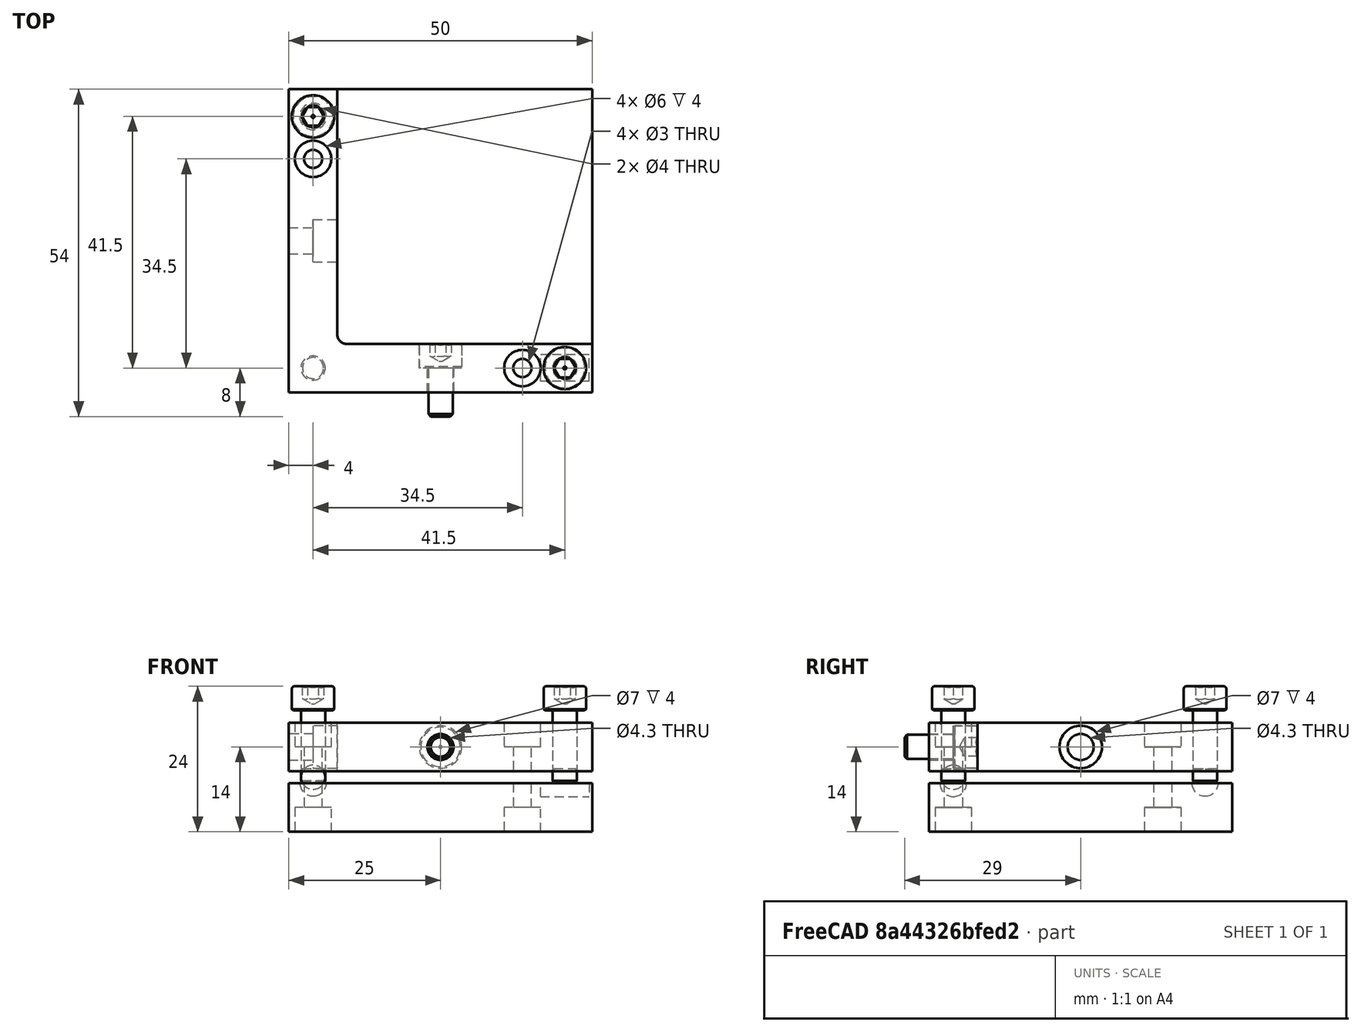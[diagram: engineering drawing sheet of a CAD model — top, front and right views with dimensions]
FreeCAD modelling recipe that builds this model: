
FCSTD DOCUMENT  (FreeCAD 0.21R33668 +7 (Git))
Label: KinematicMountBase_M4
License: All rights reserved
LicenseURL: https://en.wikipedia.org/wiki/All_rights_reserved
objects: Part::Cut×13, Part::Cylinder×13, Part::MultiFuse×6, Part::FeaturePython×5, Part::Sphere×4, Part::Box×3, Spreadsheet::Sheet×1, Part::Fillet×1
note: 45 computed .brp shape members not serialized (recipe doc carries the construction recipe); baked Part::Feature solids carry a one-line shape summary decoded from their .brp

FEATURE [Part::Box] Box  label="Cube"
  AttacherType = Attacher::AttachEngine3D
  Height = 8
  Length = 50
  Width = 50
  expr: Height = <<MountConfiguration>>.thickness
  expr: Length = <<MountConfiguration>>.outer_length
  expr: Width = <<MountConfiguration>>.outer_length
FEATURE [Spreadsheet::Sheet] Spreadsheet  label="MountConfiguration"
  cells = A2='Outer length; B2(outer_length)=50; A3='Holder width; B3(holder_width)=8; A4='Thickness; B4(thickness)=8
FEATURE [Part::Box] Box001  label="Cube001"
  AttacherType = Attacher::AttachEngine3D
  Height = 8
  Length = 42
  Placement = pos=(8,8,0) rot=(0,0,1;0rad)
  Width = 42
  expr: .Placement.Base.x = <<MountConfiguration>>.holder_width
  expr: .Placement.Base.y = <<MountConfiguration>>.holder_width
  expr: Height = <<MountConfiguration>>.thickness
  expr: Length = <<MountConfiguration>>.outer_length - <<MountConfiguration>>.holder_width
  expr: Width = <<MountConfiguration>>.outer_length - <<MountConfiguration>>.holder_width
FEATURE [Part::Cut] Cut
  Base = -> Box
  Tool = -> Box001
FEATURE [Part::FeaturePython] Screw  label="M4x8-Screw"  # Fasteners workbench fastener (typed FeaturePython)
  Placement = pos=(45.5,4,8) rot=(0,0,1;0rad)
  diameter = 5
  invert = false
  leftHanded = false
  length = 1
  lengthCustom = 8
  matchOuter = false
  offset = 0
  thread = false
  type = 47
  expr: .Placement.Base.x = <<MountConfiguration>>.outer_length - 7 / 2 - 1
  expr: .Placement.Base.y = <<MountConfiguration>>.holder_width / 2
  expr: .Placement.Base.z = <<MountConfiguration>>.thickness
FEATURE [Part::FeaturePython] Screw001  label="M4x8-Screw003"  # Fasteners workbench fastener (typed FeaturePython)
  Placement = pos=(4,45.5,8) rot=(0,0,1;0rad)
  diameter = 5
  invert = false
  leftHanded = false
  length = 1
  lengthCustom = 8
  matchOuter = false
  offset = 0
  thread = false
  type = 47
  expr: .Placement.Base.x = <<MountConfiguration>>.holder_width / 2
  expr: .Placement.Base.y = <<MountConfiguration>>.outer_length - 7 / 2 - 1
  expr: .Placement.Base.z = <<MountConfiguration>>.thickness
FEATURE [Part::Cylinder] Cylinder
  Angle = 360
  AttacherType = Attacher::AttachEngine3D
  FirstAngle = 0
  Height = 8
  Radius = 1.5
  SecondAngle = 0
  expr: Height = <<MountConfiguration>>.thickness
FEATURE [Part::Cylinder] Cylinder001
  Angle = 360
  AttacherType = Attacher::AttachEngine3D
  FirstAngle = 0
  Height = 4
  Placement = pos=(0,0,4) rot=(0,0,1;0rad)
  Radius = 3
  SecondAngle = 0
  expr: .Placement.Base.z = <<MountConfiguration>>.thickness / 2
  expr: Height = <<MountConfiguration>>.thickness / 2
FEATURE [Part::MultiFuse] Fusion  label="SpringHole1"
  Placement = pos=(38.5,4,0) rot=(0,0,1;0rad)
  Shapes = -> [Cylinder,Cylinder001]
  expr: .Placement.Base.x = <<MountConfiguration>>.outer_length - 7 / 2 - 1 - 1 * 7
  expr: .Placement.Base.y = <<MountConfiguration>>.holder_width / 2
FEATURE [Part::Cylinder] Cylinder002
  Angle = 360
  AttacherType = Attacher::AttachEngine3D
  FirstAngle = 0
  Height = 8
  Radius = 1.5
  SecondAngle = 0
  expr: Height = <<MountConfiguration>>.thickness
FEATURE [Part::Cylinder] Cylinder003
  Angle = 360
  AttacherType = Attacher::AttachEngine3D
  FirstAngle = 0
  Height = 4
  Placement = pos=(0,0,4) rot=(0,0,1;0rad)
  Radius = 3
  SecondAngle = 0
  expr: .Placement.Base.z = <<MountConfiguration>>.thickness / 2
  expr: Height = <<MountConfiguration>>.thickness / 2
FEATURE [Part::MultiFuse] Fusion001  label="SpringHole2"
  Placement = pos=(4,38.5,0) rot=(0,0,1;0rad)
  Shapes = -> [Cylinder002,Cylinder003]
  expr: .Placement.Base.x = <<MountConfiguration>>.holder_width / 2
  expr: .Placement.Base.y = <<MountConfiguration>>.outer_length - 7 / 2 - 1 - 1 * 7
FEATURE [Part::Cut] Cut001
  Base = -> Cut
  Tool = -> Fusion
FEATURE [Part::Cut] Cut002
  Base = -> Cut001
  Tool = -> Fusion001
FEATURE [Part::Cut] Cut003
  Base = -> Cut002
  Tool = -> Screw001
FEATURE [Part::Cut] Cut004
  Base = -> Cut003
  Tool = -> Screw
FEATURE [Part::FeaturePython] Screw002  label="M4x8-Screw004"  # Fasteners workbench fastener (typed FeaturePython)
  Placement = pos=(25,4,14) rot=(1,0,0;-1.5708rad)
  diameter = 5
  invert = false
  leftHanded = false
  length = 1
  lengthCustom = 8
  matchOuter = false
  offset = 0
  thread = false
  type = 47
  expr: .Placement.Base.x = <<MountConfiguration>>.outer_length / 2
  expr: .Placement.Base.y = <<MountConfiguration>>.holder_width - 4
  expr: .Placement.Base.z = <<MountConfiguration>>.thickness / 2 + <<MountConfiguration>>.thickness + 2
FEATURE [Part::Cylinder] Cylinder004
  Angle = 360
  AttacherType = Attacher::AttachEngine3D
  FirstAngle = 0
  Height = 4
  Radius = 3.5
  SecondAngle = 0
FEATURE [Part::Cylinder] Cylinder005
  Angle = 360
  AttacherType = Attacher::AttachEngine3D
  FirstAngle = 0
  Height = 8
  Radius = 2.15
  SecondAngle = 0
  expr: Height = <<MountConfiguration>>.holder_width
FEATURE [Part::MultiFuse] Fusion002
  Placement = pos=(25,8,4) rot=(0.242536,0,0;1.5708rad)
  Shapes = -> [Cylinder005,Cylinder004]
  expr: .Placement.Base.x = <<MountConfiguration>>.outer_length / 2
  expr: .Placement.Base.y = <<MountConfiguration>>.holder_width
  expr: .Placement.Base.z = <<MountConfiguration>>.thickness / 2
FEATURE [Part::Cut] Cut005
  Base = -> Cut004
  Tool = -> Fusion002
FEATURE [Part::Sphere] Sphere
  Angle1 = -90
  Angle2 = 90
  Angle3 = 360
  AttacherType = Attacher::AttachEngine3D
  Placement = pos=(4,4,-1) rot=(0,0,1;0rad)
  Radius = 2
  expr: .Placement.Base.x = <<MountConfiguration>>.holder_width / 2
  expr: .Placement.Base.y = <<MountConfiguration>>.holder_width / 2
FEATURE [Part::Cut] Cut006
  Base = -> Cut005
  Tool = -> Sphere
FEATURE [Part::Cylinder] Cylinder006
  Angle = 360
  AttacherType = Attacher::AttachEngine3D
  FirstAngle = 0
  Height = 4
  Radius = 3.5
  SecondAngle = 0
FEATURE [Part::Cylinder] Cylinder007
  Angle = 360
  AttacherType = Attacher::AttachEngine3D
  FirstAngle = 0
  Height = 8
  Radius = 2.15
  SecondAngle = 0
  expr: Height = <<MountConfiguration>>.holder_width
FEATURE [Part::MultiFuse] Fusion003
  Placement = pos=(8,25,4) rot=(0,1,0;-1.5708rad)
  Shapes = -> [Cylinder007,Cylinder006]
  expr: .Placement.Base.x = <<MountConfiguration>>.holder_width
  expr: .Placement.Base.y = <<MountConfiguration>>.outer_length / 2
  expr: .Placement.Base.z = <<MountConfiguration>>.thickness / 2
FEATURE [Part::Cut] Cut007  label="KinematicBase"
  Base = -> Cut006
  Tool = -> Fusion003
FEATURE [Part::Fillet] Fillet
  Base = -> Cut007
  Edges = 1 edges r=1.5: [Edge33]
  Placement = pos=(0,0,10) rot=(0,0,1;0rad)
  expr: .Placement.Base.z = <<MountConfiguration>>.thickness + 2
FEATURE [Part::Box] Box002  label="Cube002"
  AttacherType = Attacher::AttachEngine3D
  Height = 8
  Length = 50
  Width = 50
  expr: Height = <<MountConfiguration>>.thickness
  expr: Length = <<MountConfiguration>>.outer_length
  expr: Width = <<MountConfiguration>>.outer_length
FEATURE [Part::Cylinder] Cylinder008
  Angle = 360
  AttacherType = Attacher::AttachEngine3D
  FirstAngle = 0
  Height = 8
  Radius = 1.5
  SecondAngle = 0
  expr: Height = <<MountConfiguration>>.thickness
FEATURE [Part::Cylinder] Cylinder009
  Angle = 360
  AttacherType = Attacher::AttachEngine3D
  FirstAngle = 0
  Height = 4
  Radius = 3
  SecondAngle = 0
  expr: Height = <<MountConfiguration>>.thickness / 2
FEATURE [Part::Cylinder] Cylinder010
  Angle = 360
  AttacherType = Attacher::AttachEngine3D
  FirstAngle = 0
  Height = 8
  Radius = 1.5
  SecondAngle = 0
  expr: Height = <<MountConfiguration>>.thickness
FEATURE [Part::Cylinder] Cylinder011
  Angle = 360
  AttacherType = Attacher::AttachEngine3D
  FirstAngle = 0
  Height = 4
  Radius = 3
  SecondAngle = 0
  expr: Height = <<MountConfiguration>>.thickness / 2
FEATURE [Part::MultiFuse] Fusion004  label="SpringHole003"
  Placement = pos=(38.5,4,0) rot=(0,0,1;0rad)
  Shapes = -> [Cylinder008,Cylinder009]
  expr: .Placement.Base.x = <<MountConfiguration>>.outer_length - 7 / 2 - 1 - 1 * 7
  expr: .Placement.Base.y = <<MountConfiguration>>.holder_width / 2
FEATURE [Part::MultiFuse] Fusion005  label="SpringHole004"
  Placement = pos=(4,38.5,0) rot=(0,0,1;0rad)
  Shapes = -> [Cylinder010,Cylinder011]
  expr: .Placement.Base.x = <<MountConfiguration>>.holder_width / 2
  expr: .Placement.Base.y = <<MountConfiguration>>.outer_length - 7 / 2 - 1 - 1 * 7
FEATURE [Part::Cut] Cut008
  Base = -> Box002
  Tool = -> Fusion004
FEATURE [Part::Cut] Cut009
  Base = -> Cut008
  Tool = -> Fusion005
FEATURE [Part::Sphere] Sphere001
  Angle1 = -90
  Angle2 = 90
  Angle3 = 360
  AttacherType = Attacher::AttachEngine3D
  Placement = pos=(4,4,9) rot=(0,0,1;0rad)
  Radius = 2
  expr: .Placement.Base.x = <<MountConfiguration>>.holder_width / 2
  expr: .Placement.Base.y = <<MountConfiguration>>.holder_width / 2
  expr: .Placement.Base.z = <<MountConfiguration>>.thickness + 1
FEATURE [Part::Sphere] Sphere002  label="SteelBall"
  Angle1 = -90
  Angle2 = 90
  Angle3 = 360
  AttacherType = Attacher::AttachEngine3D
  Placement = pos=(4,4,9) rot=(0,0,1;0rad)
  Radius = 2
  expr: .Placement.Base.x = <<MountConfiguration>>.holder_width / 2
  expr: .Placement.Base.y = <<MountConfiguration>>.holder_width / 2
  expr: .Placement.Base.z = <<MountConfiguration>>.thickness + 1
FEATURE [Part::Cut] Cut010
  Base = -> Cut009
  Tool = -> Sphere001
FEATURE [Part::Sphere] Sphere003
  Angle1 = -90
  Angle2 = 90
  Angle3 = 360
  AttacherType = Attacher::AttachEngine3D
  Placement = pos=(4,45.5,8.1) rot=(0,0,1;0rad)
  Radius = 2.2
  expr: .Placement.Base.x = <<MountConfiguration>>.holder_width / 2
  expr: .Placement.Base.y = <<MountConfiguration>>.outer_length - 7 / 2 - 1
  expr: .Placement.Base.z = <<MountConfiguration>>.thickness + 0.1
FEATURE [Part::Cut] Cut011
  Base = -> Cut010
  Tool = -> Sphere003
FEATURE [Part::Cylinder] Cylinder012
  Angle = 360
  AttacherType = Attacher::AttachEngine3D
  FirstAngle = 0
  Height = 8
  Placement = pos=(41.5,4,8) rot=(0,1,0;1.5708rad)
  Radius = 2.2
  SecondAngle = 0
  expr: .Placement.Base.x = <<MountConfiguration>>.outer_length - 7 / 2 - 1 - 4
  expr: .Placement.Base.y = <<MountConfiguration>>.holder_width / 2
  expr: .Placement.Base.z = <<MountConfiguration>>.thickness
FEATURE [Part::Cut] Cut012
  Base = -> Cut011
  Tool = -> Cylinder012
FEATURE [Part::FeaturePython] Screw003  label="M4x12-Screw"  # Fasteners workbench fastener (typed FeaturePython)
  Placement = pos=(45.5,4,20) rot=(0,0,1;0rad)
  diameter = 5
  invert = false
  leftHanded = false
  length = 3
  lengthCustom = 12
  matchOuter = false
  offset = 0
  thread = false
  type = 47
  expr: .Placement.Base.x = <<MountConfiguration>>.outer_length - 7 / 2 - 1
  expr: .Placement.Base.y = <<MountConfiguration>>.holder_width / 2
  expr: .Placement.Base.z = <<MountConfiguration>>.thickness + <<MountConfiguration>>.thickness + 2 + 2
  expr: lengthCustom = <<MountConfiguration>>.thickness + 4
FEATURE [Part::FeaturePython] Screw004  label="M4x12-Screw001"  # Fasteners workbench fastener (typed FeaturePython)
  Placement = pos=(4,45.5,20) rot=(0,0,1;0rad)
  diameter = 5
  invert = false
  leftHanded = false
  length = 11
  lengthCustom = 12
  matchOuter = false
  offset = 0
  thread = false
  type = 47
  expr: .Placement.Base.x = <<MountConfiguration>>.holder_width / 2
  expr: .Placement.Base.y = <<MountConfiguration>>.outer_length - 7 / 2 - 1
  expr: .Placement.Base.z = <<MountConfiguration>>.thickness + <<MountConfiguration>>.thickness + 2 + 2
  expr: lengthCustom = <<MountConfiguration>>.thickness + 4
